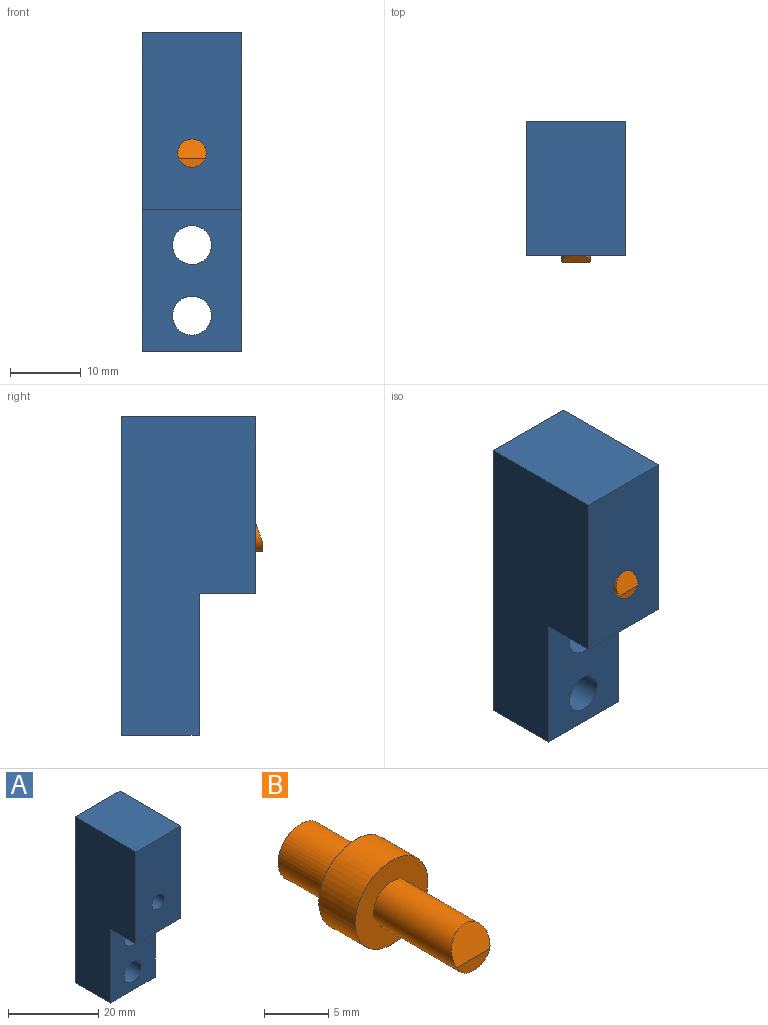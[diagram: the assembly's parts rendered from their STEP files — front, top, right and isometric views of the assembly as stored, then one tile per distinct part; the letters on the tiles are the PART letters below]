
ASSEMBLY  parts=2 mates=1
PART A: 16 faces, bbox 14x19x45 mm
  f0: plane 45x14mm, normal (0,1,0), area 433.2mm2, adj f2,f5,f7,f8,f11,f13,f14
  f1: cylinder r=2.75mm len=10mm, axis (0,-1,0), area 172.8mm2, adj f10,f15
  f2: plane 14x11mm, normal (0,0,-1), area 148mm2, adj f0,f5,f7,f10,f13,f14,f15
  f3: cylinder r=2.75mm len=10mm, axis (0,-1,0), area 172.8mm2, adj f10,f15
  f4: cylinder r=2mm len=8mm, axis (0,-1,0), area 100.5mm2, adj f6,f12
  f5: plane 45x19mm, normal (-1,0,0), area 695mm2, adj f0,f2,f6,f8,f9,f10
  f6: plane 25x14mm, normal (0,-1,0), area 337.4mm2, adj f4,f5,f7,f8,f9
  f7: plane 45x19mm, normal (1,0,0), area 695mm2, adj f0,f2,f6,f8,f9,f10
  f8: plane 19x14mm, normal (0,0,1), area 266mm2, adj f0,f5,f6,f7
  f9: plane 14x8mm, normal (0,0,-1), area 112mm2, adj f5,f6,f7,f10
  f10: plane 20x14mm, normal (0,-1,0), area 232.5mm2, adj f1,f2,f3,f5,f7,f9
  f11: cylinder r=4mm len=11mm, axis (0,1,0), area 269.7mm2, adj f0,f12,f13,f14,f15
  f12: plane 8x8mm, normal (0,1,0), area 37.7mm2, adj f4,f11
  f13: plane 25.35x1mm, normal (-1,0,0), area 25.4mm2, adj f0,f2,f11,f15
  f14: plane 25.35x1mm, normal (1,0,0), area 25.4mm2, adj f0,f2,f11,f15
  f15: plane 25.35x6mm, normal (0,1,0), area 99mm2, adj f1,f2,f3,f11,f13,f14
PART B: 8 faces, bbox 8x19x8 mm
  f0: cylinder r=2mm len=9mm, axis (0,1,0), area 108.2mm2, adj f3,f4,f7
  f1: cylinder r=4mm len=8mm, axis (0,-1,0), area 100.5mm2, adj f2,f3
  f2: plane 8x8mm, normal (0,1,0), area 30.6mm2, adj f1,f5
  f3: plane 8x8mm, normal (0,-1,0), area 37.7mm2, adj f0,f1
  f4: plane 3.69x1.2mm, normal (0,-1,0), area 3.1mm2, adj f0,f7
  f5: cylinder r=2.5mm len=6mm, axis (0,-1,0), area 94.2mm2, adj f2,f6
  f6: plane 5x5mm, normal (0,1,0), area 19.6mm2, adj f5
  f7: plane 4.01x2.83mm, normal (0,-0.94,0.33), area 10mm2, adj f0,f4
PLACE A t=(55.69,-5.43,-13.6)mm fixed
PLACE B t=(38.61,2.57,8.35)mm
MATE slider B.f0 <-> A.f4  axis (0,1,0) through (38.61,-6.43,8.35)mm
